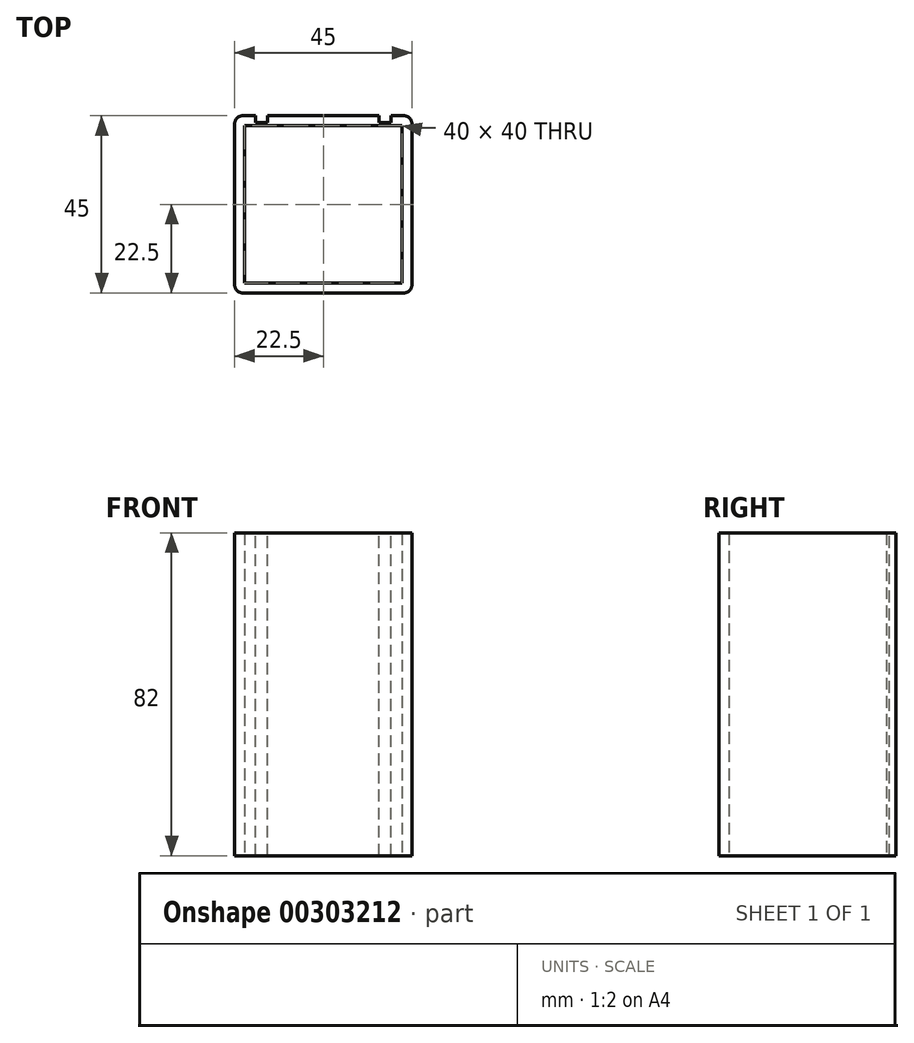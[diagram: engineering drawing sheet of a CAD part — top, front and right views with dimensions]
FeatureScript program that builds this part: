
annotation { "Feature Type Name" : "Feature", "Feature Type Description" : "" }
export const myFeature = defineFeature(function(context is Context, id is Id, definition is map)
    precondition{}
    {
        {
            var Q0;
            Q0=qCreatedBy(makeId("Top.planeOp"),FACE);
            var sketch = newSketch(context, id + "F0", { "sketchPlane" : qUnion([Q0])});
            skLineSegment(sketch, "E0.bottom", {"start": v(20.5, -22.5) * mm, "end": v(-20.5, -22.5) * mm});
            skLineSegment(sketch, "E0.top", {"start": v(20.5, 22.5) * mm, "end": v(-20.5, 22.5) * mm});
            skLineSegment(sketch, "E0.left", {"start": v(22.5, -20.5) * mm, "end": v(22.5, 20.5) * mm});
            skLineSegment(sketch, "E0.right", {"start": v(-22.5, -20.5) * mm, "end": v(-22.5, 20.5) * mm});
            skPoint(sketch, "E0.middle", {"position": v(0, 0) * mm});
            skLineSegment(sketch, "E1.0", {"start": v(20, 20) * mm, "end": v(-20, 20) * mm});
            skLineSegment(sketch, "E1.1", {"start": v(20, -20) * mm, "end": v(20, 20) * mm});
            skLineSegment(sketch, "E1.2", {"start": v(20, -20) * mm, "end": v(-20, -20) * mm});
            skLineSegment(sketch, "E1.3", {"start": v(-20, -20) * mm, "end": v(-20, 20) * mm});
            skPoint(sketch, "E2.visualSharp", {"position": v(-22.5, 22.5) * mm});
            skArc(sketch, "E2.filletArc", {"start": v(-20.5, 22.5) * mm, "mid": v(-21.91, 21.91) * mm, "end": v(-22.5, 20.5) * mm});
            skPoint(sketch, "E3.visualSharp", {"position": v(22.5, 22.5) * mm});
            skArc(sketch, "E3.filletArc", {"start": v(22.5, 20.5) * mm, "mid": v(21.91, 21.91) * mm, "end": v(20.5, 22.5) * mm});
            skPoint(sketch, "E4.visualSharp", {"position": v(22.5, -22.5) * mm});
            skArc(sketch, "E4.filletArc", {"start": v(20.5, -22.5) * mm, "mid": v(21.91, -21.91) * mm, "end": v(22.5, -20.5) * mm});
            skPoint(sketch, "E5.visualSharp", {"position": v(-22.5, -22.5) * mm});
            skArc(sketch, "E5.filletArc", {"start": v(-22.5, -20.5) * mm, "mid": v(-21.91, -21.91) * mm, "end": v(-20.5, -22.5) * mm});
            skSolve(sketch);
        }
        {
            var Q0;
            Q0=makeQuery(id+"F0.imprint","IMPRINT",FACE,{"disambiguationData":[TD([[makeQuery(id+"F0.imprint","IMPRINT",EDGE,{"derivedFrom":sQuery(id+"F0.wireOp",EDGE,"E0.bottom")}),-1.0]])]});
            extrude(context, id + "F1", {"entities" : qUnion([Q0]), "depth" : 82 * mm});
        }
        {
            var Q0;
            Q0=makeQuery(id+"F1.opExtrude","CAP_FACE",FACE,{"disambiguationData":[OSD([sQuery(id+"F0.wireOp",EDGE,"E0.bottom"),sQuery(id+"F0.wireOp",EDGE,"E0.top"),sQuery(id+"F0.wireOp",EDGE,"E0.left"),sQuery(id+"F0.wireOp",EDGE,"E0.right"),sQuery(id+"F0.wireOp",EDGE,"E1.0"),sQuery(id+"F0.wireOp",EDGE,"E1.1"),sQuery(id+"F0.wireOp",EDGE,"E1.2"),sQuery(id+"F0.wireOp",EDGE,"E1.3"),sQuery(id+"F0.wireOp",EDGE,"E2.filletArc"),sQuery(id+"F0.wireOp",EDGE,"E3.filletArc"),sQuery(id+"F0.wireOp",EDGE,"E4.filletArc"),sQuery(id+"F0.wireOp",EDGE,"E5.filletArc")])],"isStart":false});
            var sketch = newSketch(context, id + "F2", { "sketchPlane" : qUnion([Q0])});
            skLineSegment(sketch, "E6.bottom", {"start": v(14.18, 22.5) * mm, "end": v(17.18, 22.5) * mm});
            skLineSegment(sketch, "E6.top", {"start": v(14.18, 20.75) * mm, "end": v(17.18, 20.75) * mm});
            skLineSegment(sketch, "E6.left", {"start": v(14.18, 22.5) * mm, "end": v(14.18, 20.75) * mm});
            skLineSegment(sketch, "E6.right", {"start": v(17.18, 22.5) * mm, "end": v(17.18, 20.75) * mm});
            skLineSegment(sketch, "E7.bottom", {"start": v(-17.18, 22.5) * mm, "end": v(-14.18, 22.5) * mm});
            skLineSegment(sketch, "E7.top", {"start": v(-17.18, 20.75) * mm, "end": v(-14.18, 20.75) * mm});
            skLineSegment(sketch, "E7.left", {"start": v(-17.18, 22.5) * mm, "end": v(-17.18, 20.75) * mm});
            skLineSegment(sketch, "E7.right", {"start": v(-14.18, 22.5) * mm, "end": v(-14.18, 20.75) * mm});
            skSolve(sketch);
        }
        {
            var Q0;
            Q0=makeQuery(id+"F2.imprint","IMPRINT",FACE,{"disambiguationData":[TD([[makeQuery(id+"F2.imprint","IMPRINT",EDGE,{"derivedFrom":sQuery(id+"F2.wireOp",EDGE,"E7.bottom")}),1.0]])]});
            var Q1;
            Q1=makeQuery(id+"F2.imprint","IMPRINT",FACE,{"disambiguationData":[TD([[makeQuery(id+"F2.imprint","IMPRINT",EDGE,{"derivedFrom":sQuery(id+"F2.wireOp",EDGE,"E6.bottom")}),1.0]])]});
            extrude(context, id + "F3", {"entities" : qUnion([Q0, Q1]), "operationType" : NewBodyOperationType.REMOVE, "endBound" : BoundingType.UP_TO_NEXT, "oppositeDirection" : true, "depth" : 25 * mm});
        }
        {
            var Q0;
            Q0=qCreatedBy(makeId("Right.planeOp"),FACE);
            var sketch = newSketch(context, id + "F4", { "sketchPlane" : qUnion([Q0])});
            skLineSegment(sketch, "E8", {"start": v(0, 0) * mm, "end": v(0, 98.47) * mm, "construction": true});
            skSolve(sketch);
        }
    });
